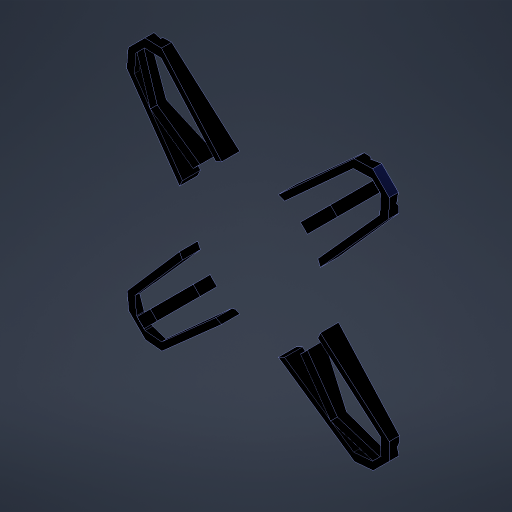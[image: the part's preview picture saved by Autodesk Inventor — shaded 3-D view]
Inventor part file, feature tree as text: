
AUTODESK INVENTOR PART (.ipt)
format: ipt  version: 2023 (Build 270158000, 158)  size: 612,864 bytes
history: native  units: mm
features: chamfer x20, extrude x8, sketch x8, fillet x3, pattern_circular x1, direct_edit x1, other x1
ambient origin geometry x8: Origin, YZ Plane, XZ Plane, XY Plane, X Axis, Y Axis, Z Axis, Center Point
bodies: Solid1 (feature_tree)
feature tree (42):
  extrude  "Extrusion1"  Depth=30.0mm
  fillet  "Fillet1"  Radius=30.0mm
  extrude  "Extrusion2"  Depth=30.0mm
  extrude  "Extrusion3"  Depth=30.0mm
  chamfer  "Chamfer1"  Distance=10.0mm
  extrude  "Extrusion4"  Depth=15.0mm
  chamfer  "Chamfer2"  Distance=15.0mm
  chamfer  "Chamfer3"  Distance=25.0mm
  chamfer  "Chamfer4"  Distance=85.0mm
  chamfer  "Chamfer5"  Distance=25.0mm
  chamfer  "Chamfer6"  Distance=85.0mm
  chamfer  "Chamfer7"  Distance=8.37758mm
  chamfer  "Chamfer8"  Distance=5.0mm
  chamfer  "Chamfer9"  Distance=40.0mm Angle=360.0deg
  extrude  "Extrusion5"  Depth=15.0mm TaperAngle=0.0deg
  pattern_circular  "Circular Pattern1"  Angle=45.0deg  [1 undecoded]
  chamfer  "Chamfer12"  Distance=40.0mm Angle=360.0deg
  chamfer  "Chamfer13"  Distance=20.0mm
  chamfer  "Chamfer14"  Distance=42.5mm Angle=45.0deg
  chamfer  "Chamfer15"  Distance=42.5mm Angle=45.0deg
  chamfer  "Chamfer18"  Distance=42.5mm Angle=45.0deg
  chamfer  "Chamfer19"  Distance=42.5mm Angle=45.0deg
  fillet  "Fillet2"  Radius=32.44mm
  fillet  "Fillet3"  Radius=32.44mm
  chamfer  "Chamfer20"  Distance=32.44mm Angle=45.0deg
  chamfer  "Chamfer21"  Distance=32.44mm Angle=45.0deg
  chamfer  "Chamfer22"  Distance=7.5mm
  chamfer  "Chamfer23"  Distance=8.1mm
  chamfer  "Chamfer24"  Distance=40.0mm Angle=360.0deg
  extrude  "Extrusion6"  Depth=10.0mm TaperAngle=45.0deg
  direct_edit  "Direct Edit2"
  extrude  "Extrusion7"  Depth=10.0mm TaperAngle=45.0deg
  extrude  "Extrusion8"  Depth=10.0mm TaperAngle=45.0deg
  sketch  "Sketch1"  dims[d0=200.0mm d1=200.0mm d2=30.0mm]
  sketch  "Sketch2"  dims[d3=30.0mm d4=30.0mm]
  sketch  "Sketch3"  dims[d5=30.0mm d6=30.0mm]
  sketch  "Sketch5"  dims[d7=30.0mm]
  sketch  "Sketch6"  dims[d8=30.0mm]
  sketch  "Sketch7"  dims[d9=30.0mm d10=10.0mm d11=0.0mm]
  sketch  "Sketch8"  dims[d12=10.0mm d13=125.0mm d14=15.0mm d15=0.0mm]
  sketch  "Sketch9"  dims[d16=45.0deg d17=25.0mm d18=85.0mm d20=25.0mm d21=85.0mm d22=8.37758mm d23=5.0mm d24=40.0mm d26=360.0deg d28=15.0mm d29=0.0mm d30=85.0mm d31=7.5mm d32=45.0deg d33=40.0mm d35=360.0deg d37=20.0mm d38=0.0mm d39=42.5mm d40=5.3mm d41=45.0deg d42=42.5mm d43=5.3mm d44=45.0deg d45=42.5mm d46=5.3mm d47=45.0deg d48=42.5mm d49=5.3mm d50=45.0deg d51=32.44mm d52=12.0mm d53=45.0deg d54=32.44mm d55=12.0mm d56=45.0deg d57=32.44mm d58=12.0mm d59=45.0deg d60=32.44mm d61=12.0mm d62=45.0deg d63=7.5mm d64=8.1mm d65=0.0mm d72=40.0mm d73=360.0deg d75=1.669mm d76=5.0mm d77=45.0deg d78=1.669mm d79=5.0mm d80=45.0deg d81=1.669mm d82=5.0mm d83=45.0deg d84=1.669mm d85=5.0mm d86=45.0deg d93=1.669mm d94=5.0mm d95=45.0deg d96=1.669mm d97=5.0mm d98=45.0deg d99=7.0mm d100=6.735mm d101=10.0mm d102=5.0mm d103=45.0deg d104=1.5mm d105=5.0mm d106=45.0deg d107=1.669mm d108=5.0mm d109=45.0deg d110=1.669mm d111=5.0mm d112=45.0deg d113=10.0mm d114=5.0mm d115=45.0deg d116=200.0mm d117=0.0mm d124=15.0mm d125=10.0mm d126=10.0mm d128=3.0mm d129=3.0mm d130=3.0mm d131=3.0mm d132=200.0mm d133=0.0mm d134=350.0mm d135=0.0mm d66=0.5mm d67=0.872665mm]
  other  "Scale2"
note: 1 required parameter value undecoded (feature->parameter linkage not recoverable at this tier; creation-order binding heuristic only, values carry confidence <= 0.55)
